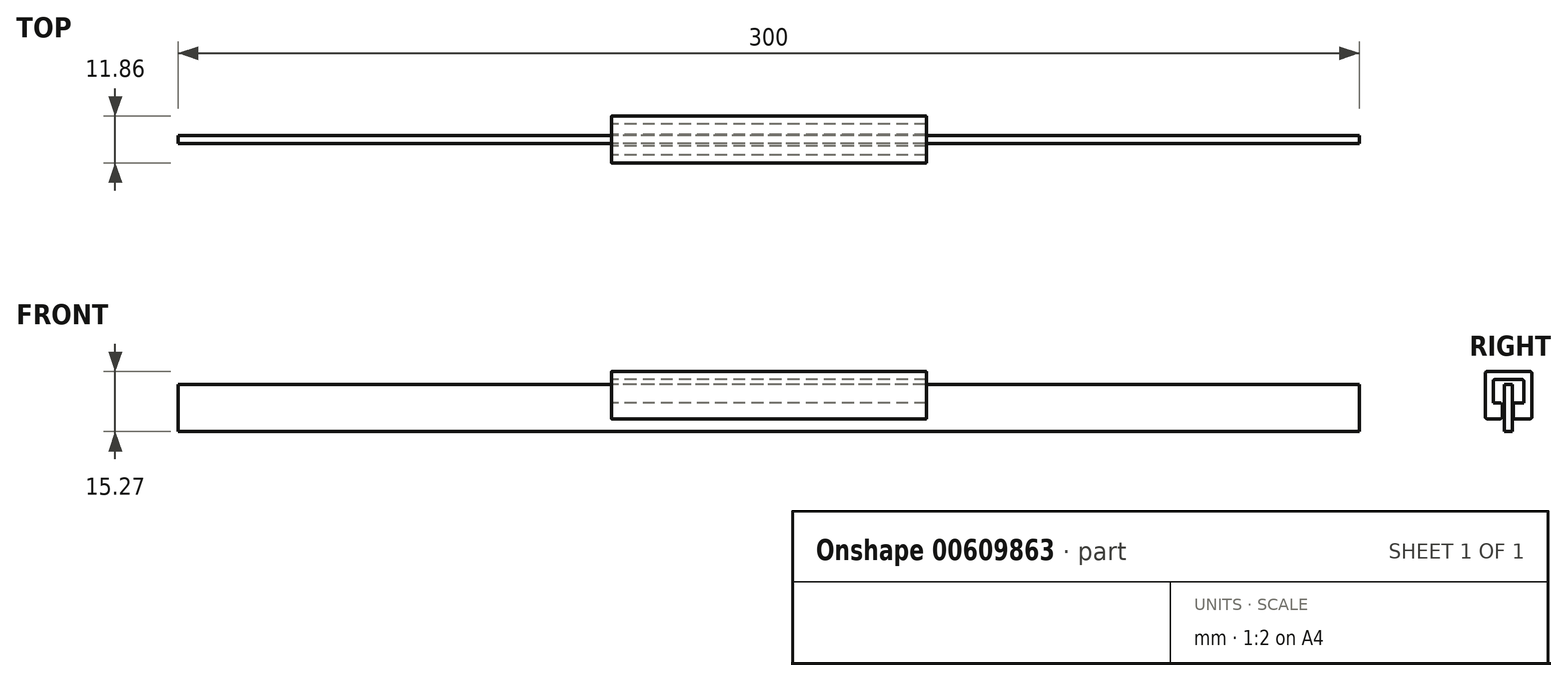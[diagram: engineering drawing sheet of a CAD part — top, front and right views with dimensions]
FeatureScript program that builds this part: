
annotation { "Feature Type Name" : "Feature", "Feature Type Description" : "" }
export const myFeature = defineFeature(function(context is Context, id is Id, definition is map)
    precondition{}
    {
        {
            var Q0;
            Q0=qCreatedBy(makeId("Right.planeOp"),FACE);
            var sketch = newSketch(context, id + "F0", { "sketchPlane" : qUnion([Q0])});
            skLineSegment(sketch, "E0.bottom", {"start": v(1, -6) * mm, "end": v(-1, -6) * mm});
            skLineSegment(sketch, "E0.top", {"start": v(1, 6) * mm, "end": v(-1, 6) * mm});
            skLineSegment(sketch, "E0.left", {"start": v(1, -6) * mm, "end": v(1, 6) * mm});
            skLineSegment(sketch, "E0.right", {"start": v(-1, -6) * mm, "end": v(-1, 6) * mm});
            skPoint(sketch, "E0.middle", {"position": v(0, 0) * mm});
            skSolve(sketch);
        }
        {
            var Q0;
            Q0=makeQuery(id+"F0.imprint","IMPRINT",FACE,{"disambiguationData":[TD([[makeQuery(id+"F0.imprint","IMPRINT",EDGE,{"derivedFrom":sQuery(id+"F0.wireOp",EDGE,"E0.bottom")}),-1.0]])]});
            extrude(context, id + "F1", {"entities" : qUnion([Q0]), "endBound" : BoundingType.SYMMETRIC, "depth" : 300 * mm, "offsetDistance" : 25 * mm});
        }
        {
            var Q0;
            Q0=qCreatedBy(makeId("Right.planeOp"),FACE);
            var sketch = newSketch(context, id + "F2", { "sketchPlane" : qUnion([Q0])});
            skLineSegment(sketch, "E1", {"start": v(-1.16, -3) * mm, "end": v(-1.16, 4.9) * mm});
            skLineSegment(sketch, "E2", {"start": v(1.16, 4.9) * mm, "end": v(1.16, -3) * mm});
            skArc(sketch, "E3", {"start": v(1.28, 5.56) * mm, "mid": v(0, 7.35) * mm, "end": v(-1.28, 5.56) * mm});
            skPoint(sketch, "E4.visualSharp", {"position": v(-1.16, 5.31) * mm});
            skArc(sketch, "E4.filletArc", {"start": v(-1.16, 4.9) * mm, "mid": v(-1.2, 5.23) * mm, "end": v(-1.28, 5.56) * mm});
            skPoint(sketch, "E5.visualSharp", {"position": v(1.16, 5.31) * mm});
            skArc(sketch, "E5.filletArc", {"start": v(1.28, 5.56) * mm, "mid": v(1.2, 5.23) * mm, "end": v(1.16, 4.9) * mm});
            skLineSegment(sketch, "E6", {"start": v(-1.16, -3) * mm, "end": v(1.16, -3) * mm});
            skSolve(sketch);
        }
        {
            var Q0;
            Q0=sQuery(id+"F2.wireOp",EDGE,"E3");
            var Q1;
            Q1=sQuery(id+"F2.wireOp",EDGE,"E4.filletArc");
            var Q2;
            Q2=sQuery(id+"F2.wireOp",EDGE,"E5.filletArc");
            var Q3;
            Q3=sQuery(id+"F2.wireOp",EDGE,"E1");
            var Q4;
            Q4=sQuery(id+"F2.wireOp",EDGE,"E2");
            extrude(context, id + "F3", {"bodyType" : ToolBodyType.SURFACE, "surfaceEntities" : qUnion([Q0, Q1, Q2, Q3, Q4]), "endBound" : BoundingType.SYMMETRIC, "depth" : 290 * mm, "offsetDistance" : 25 * mm});
        }
        {
            var Q0;
            Q0=qCreatedBy(makeId("Right.planeOp"),FACE);
            var sketch = newSketch(context, id + "F4", { "sketchPlane" : qUnion([Q0])});
            skLineSegment(sketch, "E7", {"start": v(-2.12, 1.27) * mm, "end": v(-3.92, 1.27) * mm});
            skLineSegment(sketch, "E8", {"start": v(-3.92, 1.27) * mm, "end": v(-3.92, 6.77) * mm});
            skLineSegment(sketch, "E9", {"start": v(-3.42, 7.27) * mm, "end": v(3.42, 7.27) * mm});
            skLineSegment(sketch, "E10", {"start": v(3.92, 6.77) * mm, "end": v(3.92, 1.27) * mm});
            skLineSegment(sketch, "E11", {"start": v(3.92, 1.27) * mm, "end": v(1.74, 1.27) * mm});
            skLineSegment(sketch, "E12", {"start": v(-2.12, -2.73) * mm, "end": v(-5.43, -2.73) * mm});
            skLineSegment(sketch, "E13", {"start": v(-5.93, -2.23) * mm, "end": v(-5.93, 8.77) * mm});
            skLineSegment(sketch, "E14", {"start": v(-5.43, 9.27) * mm, "end": v(5.43, 9.27) * mm});
            skLineSegment(sketch, "E15", {"start": v(5.93, 8.77) * mm, "end": v(5.93, -2.23) * mm});
            skLineSegment(sketch, "E16", {"start": v(5.43, -2.73) * mm, "end": v(1.24, -2.73) * mm});
            skLineSegment(sketch, "E17", {"start": v(0, 0) * mm, "end": v(0, 14.26) * mm, "construction": true});
            skLineSegment(sketch, "E18", {"start": v(-1.62, 1.27) * mm, "end": v(-1.62, -2.73) * mm});
            skLineSegment(sketch, "E19", {"start": v(-1.62, 0.77) * mm, "end": v(-1.62, -2.23) * mm});
            skLineSegment(sketch, "E20", {"start": v(-1.62, -2.73) * mm, "end": v(-1.62, 1.27) * mm});
            skPoint(sketch, "E21.visualSharp", {"position": v(-1.62, -2.73) * mm});
            skArc(sketch, "E21.filletArc", {"start": v(-2.12, -2.73) * mm, "mid": v(-1.77, -2.59) * mm, "end": v(-1.62, -2.23) * mm});
            skPoint(sketch, "E22.visualSharp", {"position": v(-1.62, 1.27) * mm});
            skArc(sketch, "E22.filletArc", {"start": v(-1.62, 0.77) * mm, "mid": v(-1.77, 1.12) * mm, "end": v(-2.12, 1.27) * mm});
            skPoint(sketch, "E23.visualSharp", {"position": v(-5.93, 9.27) * mm});
            skArc(sketch, "E23.filletArc", {"start": v(-5.43, 9.27) * mm, "mid": v(-5.79, 9.12) * mm, "end": v(-5.93, 8.77) * mm});
            skPoint(sketch, "E24.visualSharp", {"position": v(-5.93, -2.73) * mm});
            skArc(sketch, "E24.filletArc", {"start": v(-5.93, -2.23) * mm, "mid": v(-5.79, -2.59) * mm, "end": v(-5.43, -2.73) * mm});
            skPoint(sketch, "E25.visualSharp", {"position": v(5.93, 9.27) * mm});
            skArc(sketch, "E25.filletArc", {"start": v(5.93, 8.77) * mm, "mid": v(5.79, 9.12) * mm, "end": v(5.43, 9.27) * mm});
            skPoint(sketch, "E26.visualSharp", {"position": v(5.93, -2.73) * mm});
            skArc(sketch, "E26.filletArc", {"start": v(5.43, -2.73) * mm, "mid": v(5.79, -2.59) * mm, "end": v(5.93, -2.23) * mm});
            skLineSegment(sketch, "E27", {"start": v(1.24, -2.73) * mm, "end": v(1.24, 0.77) * mm});
            skPoint(sketch, "E28.visualSharp", {"position": v(1.24, 1.27) * mm});
            skArc(sketch, "E28.filletArc", {"start": v(1.74, 1.27) * mm, "mid": v(1.38, 1.12) * mm, "end": v(1.24, 0.77) * mm});
            skPoint(sketch, "E29.visualSharp", {"position": v(-3.92, 7.27) * mm});
            skArc(sketch, "E29.filletArc", {"start": v(-3.42, 7.27) * mm, "mid": v(-3.77, 7.12) * mm, "end": v(-3.92, 6.77) * mm});
            skPoint(sketch, "E30.visualSharp", {"position": v(3.92, 7.27) * mm});
            skArc(sketch, "E30.filletArc", {"start": v(3.92, 6.77) * mm, "mid": v(3.77, 7.12) * mm, "end": v(3.42, 7.27) * mm});
            skSolve(sketch);
        }
        {
            var Q0;
            Q0=qSketchRegion(id+"F4",true);
            extrude(context, id + "F5", {"entities" : qUnion([Q0]), "endBound" : BoundingType.SYMMETRIC, "depth" : 80 * mm, "offsetDistance" : 25 * mm});
        }
        {
            var Q0;
            Q0=makeQuery(id+"F5.opExtrude","SWEPT_BODY",BODY,{"disambiguationData":[OSD([sQuery(id+"F4.wireOp",EDGE,"E7"),sQuery(id+"F4.wireOp",EDGE,"E8"),sQuery(id+"F4.wireOp",EDGE,"E9"),sQuery(id+"F4.wireOp",EDGE,"E10"),sQuery(id+"F4.wireOp",EDGE,"E11"),sQuery(id+"F4.wireOp",EDGE,"E12"),sQuery(id+"F4.wireOp",EDGE,"E13"),sQuery(id+"F4.wireOp",EDGE,"E14"),sQuery(id+"F4.wireOp",EDGE,"E15"),sQuery(id+"F4.wireOp",EDGE,"E16"),sQuery(id+"F4.wireOp",EDGE,"E20"),sQuery(id+"F4.wireOp",EDGE,"E21.filletArc"),sQuery(id+"F4.wireOp",EDGE,"E22.filletArc"),sQuery(id+"F4.wireOp",EDGE,"E23.filletArc"),sQuery(id+"F4.wireOp",EDGE,"E24.filletArc"),sQuery(id+"F4.wireOp",EDGE,"E25.filletArc"),sQuery(id+"F4.wireOp",EDGE,"E26.filletArc"),sQuery(id+"F4.wireOp",EDGE,"E27"),sQuery(id+"F4.wireOp",EDGE,"E28.filletArc"),sQuery(id+"F4.wireOp",EDGE,"E29.filletArc"),sQuery(id+"F4.wireOp",EDGE,"E30.filletArc")])]});
            transform(context, id + "F6", {"entities" : qUnion([Q0]), "transformType" : TransformType.TRANSLATION_3D, "dx" : 0 * mm, "dy" : 0 * mm, "dz" : 0 * mm, "makeCopy" : true});
        }
    });
